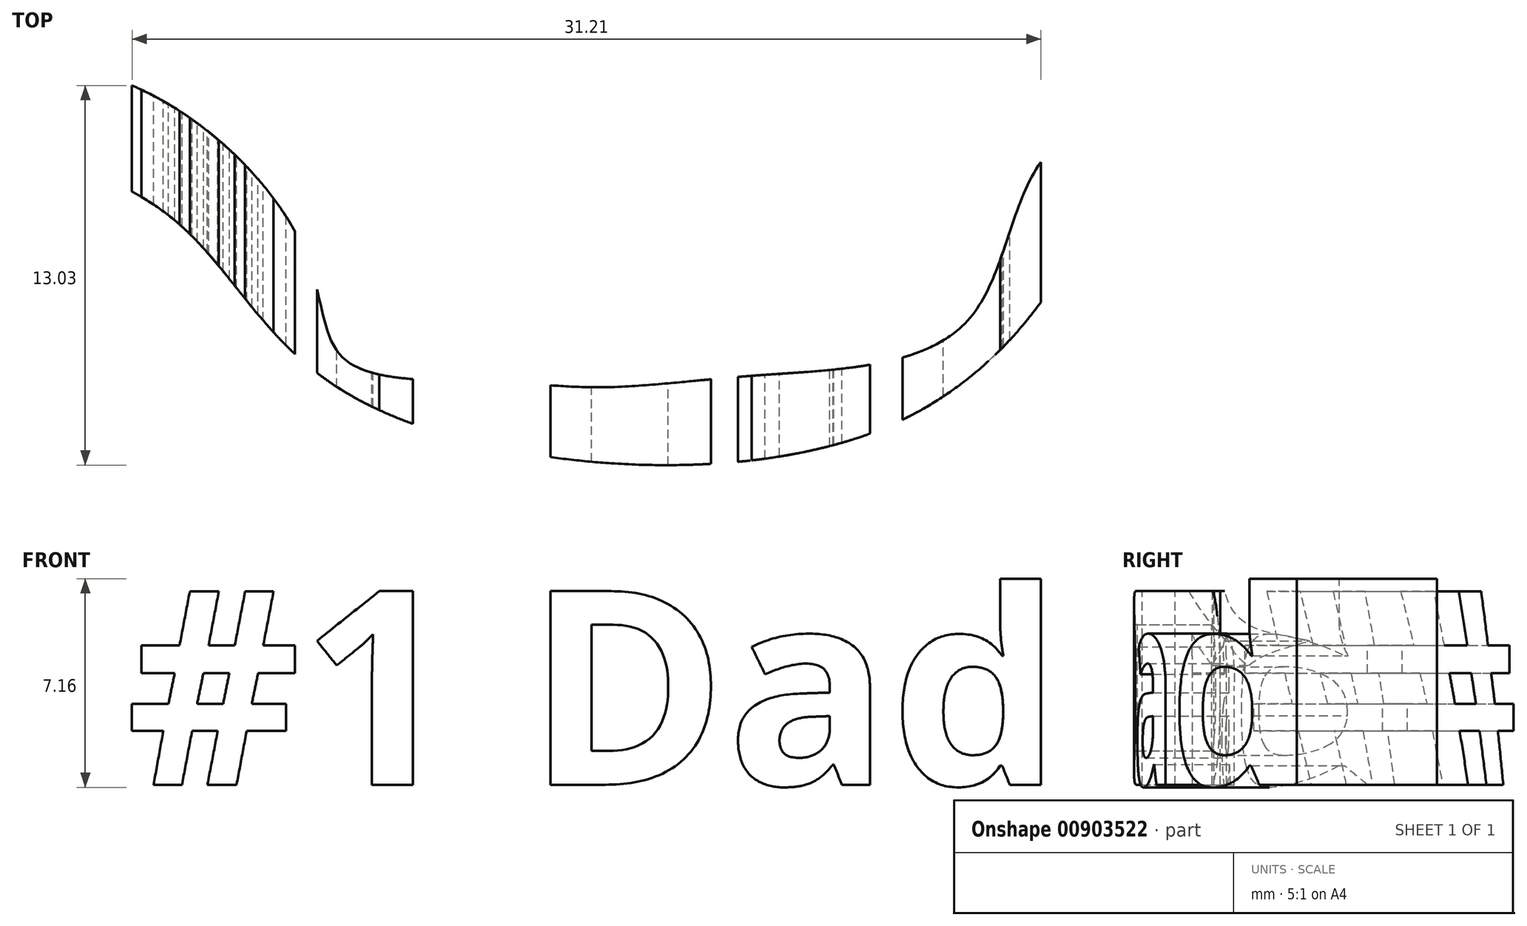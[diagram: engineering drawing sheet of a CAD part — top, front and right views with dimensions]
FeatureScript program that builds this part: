
annotation { "Feature Type Name" : "Feature", "Feature Type Description" : "" }
export const myFeature = defineFeature(function(context is Context, id is Id, definition is map)
    precondition{}
    {
        {
            var Q0;
            Q0=qCreatedBy(makeId("Front.planeOp"),FACE);
            var sketch = newSketch(context, id + "F0", { "sketchPlane" : qUnion([Q0])});
            skText(sketch, "E0", { "text": "#1 Dad", "fontName": "OpenSans-Bold.ttf"});
            const initialGuessF0  = {"E0": [-0.0148, -0.00266, 1, 0, 0.0067]};
            skSetInitialGuess(sketch, initialGuessF0);
            skSolve(sketch);
        }
        {
            var Q0;
            Q0 = qSketchRegion(id + "F0", true);
            extrude(context, id + "F1", {"entities" : qUnion([Q0]), "endBound" : BoundingType.SYMMETRIC, "depth" : 20 * mm, "offsetDistance" : 25.4 * mm});
        }
        {
            var Q0;
            Q0=qCreatedBy(makeId("Top.planeOp"),FACE);
            var sketch = newSketch(context, id + "F2", { "sketchPlane" : qUnion([Q0])});
            skFitSpline(sketch, "E1", {"points": [v(-26, 6.64) * mm, v(-13.36, 2.51) * mm, v(-7.24, -3.6) * mm, v(10.76, -5) * mm, v(17.9, 1.58) * mm, v(20.99, 4.82) * mm, v(31, 6.58) * mm], "startDerivative": vector(84.23, -21.55) * mm, "endDerivative": vector(20.96, 40.91) * mm});
            skLineSegment(sketch, "E2", {"start": v(-26, 6.64) * mm, "end": v(-27.58, -10.48) * mm});
            skLineSegment(sketch, "E3", {"start": v(-27.58, -10.48) * mm, "end": v(29.38, -10.48) * mm});
            skLineSegment(sketch, "E4", {"start": v(29.38, -10.48) * mm, "end": v(31, 6.58) * mm});
            skFitSpline(sketch, "E5", {"points": [v(-24.38, 9.74) * mm, v(-15.78, 7.37) * mm, v(-8.65, 1.22) * mm, v(-7.26, -2.47) * mm, v(-2.48, -3.2) * mm, v(1.47, -3.4) * mm, v(6.98, -3) * mm, v(14, -1.24) * mm, v(16.74, 4.5) * mm, v(22.27, 6.4) * mm, v(27.08, 7.22) * mm], "startDerivative": vector(48.8, -59.73) * mm, "endDerivative": vector(41.25, 56.87) * mm});
            skLineSegment(sketch, "E6", {"start": v(27.08, 7.22) * mm, "end": v(26.52, 11.48) * mm});
            skLineSegment(sketch, "E7", {"start": v(26.52, 11.48) * mm, "end": v(-24.38, 9.74) * mm});
            skSolve(sketch);
        }
        {
            var Q0;
            Q0=makeQuery(id+"F2.imprint","IMPRINT",FACE,{"disambiguationData":[TD([[makeQuery(id+"F2.imprint","IMPRINT",EDGE,{"derivedFrom":sQuery(id+"F2.wireOp",EDGE,"E1")}),-1.0]])]});
            extrude(context, id + "F3", {"entities" : qUnion([Q0]), "operationType" : NewBodyOperationType.REMOVE, "endBound" : BoundingType.SYMMETRIC, "oppositeDirection" : true, "depth" : 25.4 * mm, "offsetDistance" : 25.4 * mm});
        }
        {
            var Q0;
            Q0=makeQuery(id+"F2.imprint","IMPRINT",FACE,{"disambiguationData":[TD([[makeQuery(id+"F2.imprint","IMPRINT",EDGE,{"derivedFrom":sQuery(id+"F2.wireOp",EDGE,"E5")}),1.0]])]});
            extrude(context, id + "F4", {"entities" : qUnion([Q0]), "operationType" : NewBodyOperationType.REMOVE, "endBound" : BoundingType.SYMMETRIC, "oppositeDirection" : true, "depth" : 25.4 * mm, "offsetDistance" : 25.4 * mm});
        }
    });
